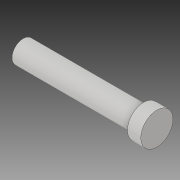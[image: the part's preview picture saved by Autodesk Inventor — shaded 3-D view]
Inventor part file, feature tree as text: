
AUTODESK INVENTOR PART (.ipt)
format: ipt  version: 2017 (Build 210142000, 142)  size: 84,480 bytes
history: native  units: mm
features: extrude x2, sketch x2, thicken_offset x1
ambient origin geometry x8: Origin, YZ Plane, XZ Plane, XY Plane, X Axis, Y Axis, Z Axis, Center Point
bodies: Solid1 (feature_tree)
feature tree (5):
  extrude  "Extrusion1"  Depth=40.0mm TaperAngle=0.0deg
  extrude  "Extrusion2"  Depth=10.0mm
  thicken_offset  "Thicken1"
  sketch  "Sketch1"  dims[d0=8.3mm d1=40.0mm d2=0.0mm]
  sketch  "Sketch2"  dims[d3=5.0mm d4=0.0mm d5=10.0mm d6=10.0mm]
